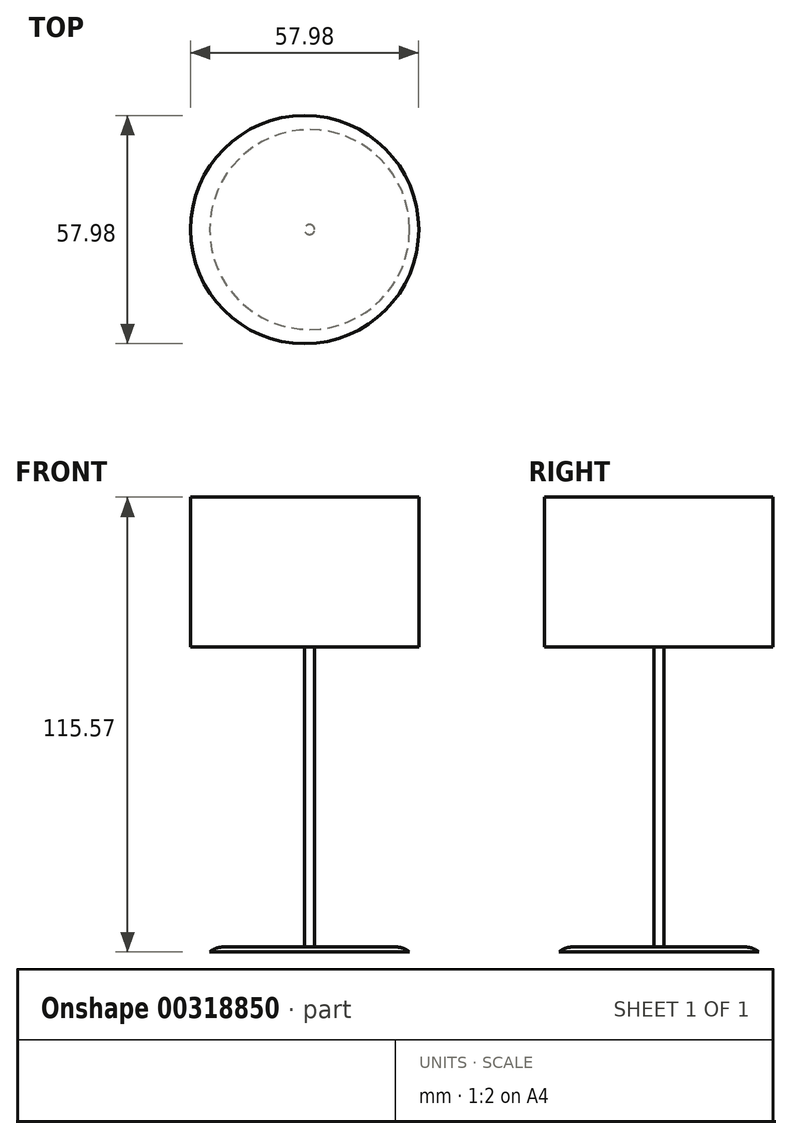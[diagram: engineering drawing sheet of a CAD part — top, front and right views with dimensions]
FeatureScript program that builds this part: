
annotation { "Feature Type Name" : "Feature", "Feature Type Description" : "" }
export const myFeature = defineFeature(function(context is Context, id is Id, definition is map)
    precondition{}
    {
        {
            var Q0;
            Q0=qCreatedBy(makeId("Top.planeOp"),FACE);
            var sketch = newSketch(context, id + "F0", { "sketchPlane" : qUnion([Q0])});
            skCircle(sketch, "E0", {"center": v(0, 0) * mm, "radius": 25.4 * mm});
            skSolve(sketch);
        }
        {
            var Q0;
            Q0 = qSketchRegion(id + "F0", true);
            extrude(context, id + "F1", {"entities" : qUnion([Q0]), "depth" : 1.27 * mm});
        }
        {
            var Q0;
            Q0=makeQuery(id+"F1.opExtrude","CAP_EDGE",EDGE,{"disambiguationData":[OSD([sQuery(id+"F0.wireOp",EDGE,"E0")])],"isStart":false});
            fillet(context, id + "F2", {"entities" : qUnion([Q0]), "radius" : 5.08 * mm, "tangentPropagation" : true, "allowEdgeOverflow" : false});
        }
        {
            var Q0;
            Q0=makeQuery(id+"F1.opExtrude","CAP_FACE",FACE,{"disambiguationData":[OSD([sQuery(id+"F0.wireOp",EDGE,"E0")])],"isStart":false});
            var sketch = newSketch(context, id + "F3", { "sketchPlane" : qUnion([Q0])});
            skCircle(sketch, "E1", {"center": v(0, 0) * mm, "radius": 1.27 * mm});
            skSolve(sketch);
        }
        {
            var Q0;
            Q0 = qSketchRegion(id + "F3", true);
            extrude(context, id + "F4", {"entities" : qUnion([Q0]), "operationType" : NewBodyOperationType.ADD, "depth" : 76.2 * mm});
        }
        {
            var Q0;
            Q0=makeQuery(id+"F4.opExtrude","CAP_FACE",FACE,{"disambiguationData":[OSD([sQuery(id+"F3.wireOp",EDGE,"E1")])],"isStart":false});
            var sketch = newSketch(context, id + "F5", { "sketchPlane" : qUnion([Q0])});
            skCircle(sketch, "E2", {"center": v(-1.27, 0) * mm, "radius": 29 * mm});
            skSolve(sketch);
        }
        {
            var Q0;
            Q0 = qSketchRegion(id + "F5", true);
            extrude(context, id + "F6", {"entities" : qUnion([Q0]), "operationType" : NewBodyOperationType.ADD, "depth" : 38.1 * mm});
        }
    });
